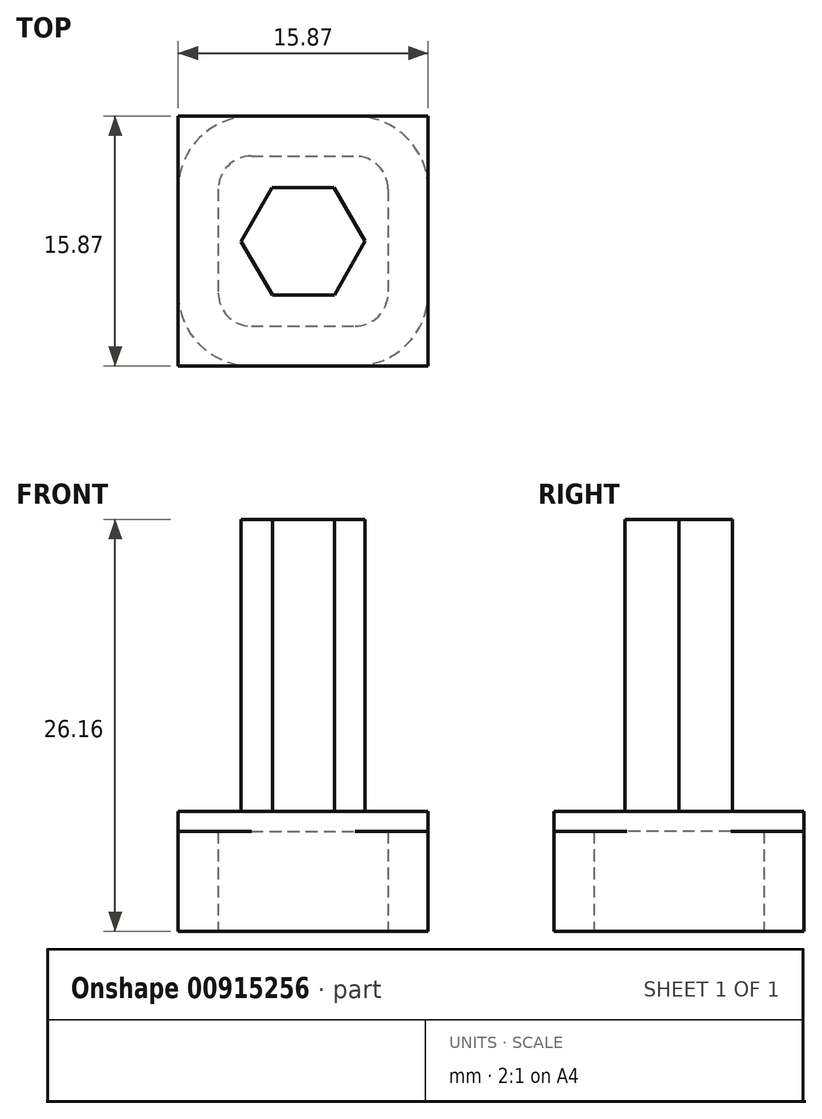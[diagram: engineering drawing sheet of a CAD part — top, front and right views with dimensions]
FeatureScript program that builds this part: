
annotation { "Feature Type Name" : "Feature", "Feature Type Description" : "" }
export const myFeature = defineFeature(function(context is Context, id is Id, definition is map)
    precondition{}
    {
        {
            var Q0;
            Q0=qCreatedBy(makeId("Top.planeOp"),FACE);
            var sketch = newSketch(context, id + "F0", { "sketchPlane" : qUnion([Q0])});
            skLineSegment(sketch, "E0.bottom", {"start": v(2.09, 6.62) * mm, "end": v(8.66, 6.62) * mm});
            skLineSegment(sketch, "E0.top", {"start": v(2.09, -9.25) * mm, "end": v(8.66, -9.25) * mm});
            skLineSegment(sketch, "E0.left", {"start": v(-2.56, 1.97) * mm, "end": v(-2.56, -4.6) * mm});
            skLineSegment(sketch, "E0.right", {"start": v(13.31, 1.97) * mm, "end": v(13.31, -4.6) * mm});
            skPoint(sketch, "E1.visualSharp", {"position": v(-2.56, 6.62) * mm});
            skArc(sketch, "E1.filletArc", {"start": v(2.09, 6.62) * mm, "mid": v(-1.2, 5.26) * mm, "end": v(-2.56, 1.97) * mm});
            skPoint(sketch, "E2.visualSharp", {"position": v(13.31, 6.62) * mm});
            skArc(sketch, "E2.filletArc", {"start": v(13.31, 1.97) * mm, "mid": v(11.95, 5.26) * mm, "end": v(8.66, 6.62) * mm});
            skPoint(sketch, "E3.visualSharp", {"position": v(13.31, -9.25) * mm});
            skArc(sketch, "E3.filletArc", {"start": v(8.66, -9.25) * mm, "mid": v(11.95, -7.9) * mm, "end": v(13.31, -4.6) * mm});
            skPoint(sketch, "E4.visualSharp", {"position": v(-2.56, -9.25) * mm});
            skArc(sketch, "E4.filletArc", {"start": v(-2.56, -4.6) * mm, "mid": v(-1.2, -7.9) * mm, "end": v(2.09, -9.25) * mm});
            skArc(sketch, "E5.0", {"start": v(2.09, 4.08) * mm, "mid": v(0.6, 3.46) * mm, "end": v(-0.02, 1.97) * mm});
            skLineSegment(sketch, "E5.1", {"start": v(-0.02, 1.97) * mm, "end": v(-0.02, -4.6) * mm});
            skLineSegment(sketch, "E5.2", {"start": v(2.09, 4.08) * mm, "end": v(8.66, 4.08) * mm});
            skArc(sketch, "E5.3", {"start": v(-0.02, -4.6) * mm, "mid": v(0.6, -6.1) * mm, "end": v(2.09, -6.71) * mm});
            skArc(sketch, "E5.4", {"start": v(10.77, 1.97) * mm, "mid": v(10.16, 3.46) * mm, "end": v(8.66, 4.08) * mm});
            skLineSegment(sketch, "E5.5", {"start": v(10.77, 1.97) * mm, "end": v(10.77, -4.6) * mm});
            skArc(sketch, "E5.6", {"start": v(8.66, -6.71) * mm, "mid": v(10.16, -6.1) * mm, "end": v(10.77, -4.6) * mm});
            skLineSegment(sketch, "E5.7", {"start": v(2.09, -6.71) * mm, "end": v(8.66, -6.71) * mm});
            skSolve(sketch);
        }
        {
            var Q0;
            Q0=makeQuery(id+"F0.imprint","IMPRINT",FACE,{"disambiguationData":[TD([[makeQuery(id+"F0.imprint","IMPRINT",EDGE,{"derivedFrom":sQuery(id+"F0.wireOp",EDGE,"E0.bottom")}),-1.0]])]});
            extrude(context, id + "F1", {"entities" : qUnion([Q0]), "depth" : 6.35 * mm, "offsetDistance" : 25.4 * mm});
        }
        {
            var Q0;
            Q0=makeQuery(id+"F1.opExtrude","CAP_FACE",FACE,{"disambiguationData":[OSD([sQuery(id+"F0.wireOp",EDGE,"E0.bottom"),sQuery(id+"F0.wireOp",EDGE,"E0.top"),sQuery(id+"F0.wireOp",EDGE,"E0.left"),sQuery(id+"F0.wireOp",EDGE,"E0.right"),sQuery(id+"F0.wireOp",EDGE,"E1.filletArc"),sQuery(id+"F0.wireOp",EDGE,"E2.filletArc"),sQuery(id+"F0.wireOp",EDGE,"E3.filletArc"),sQuery(id+"F0.wireOp",EDGE,"E4.filletArc"),sQuery(id+"F0.wireOp",EDGE,"E5.0"),sQuery(id+"F0.wireOp",EDGE,"E5.1"),sQuery(id+"F0.wireOp",EDGE,"E5.2"),sQuery(id+"F0.wireOp",EDGE,"E5.3"),sQuery(id+"F0.wireOp",EDGE,"E5.4"),sQuery(id+"F0.wireOp",EDGE,"E5.5"),sQuery(id+"F0.wireOp",EDGE,"E5.6"),sQuery(id+"F0.wireOp",EDGE,"E5.7")])],"isStart":false});
            var sketch = newSketch(context, id + "F2", { "sketchPlane" : qUnion([Q0])});
            skLineSegment(sketch, "E6.bottom", {"start": v(-2.56, 6.62) * mm, "end": v(13.31, 6.62) * mm});
            skLineSegment(sketch, "E6.top", {"start": v(-2.56, -9.25) * mm, "end": v(13.31, -9.25) * mm});
            skLineSegment(sketch, "E6.left", {"start": v(-2.56, 6.62) * mm, "end": v(-2.56, -9.25) * mm});
            skLineSegment(sketch, "E6.right", {"start": v(13.31, 6.62) * mm, "end": v(13.31, -9.25) * mm});
            skSolve(sketch);
        }
        {
            var Q0;
            Q0=makeQuery(id+"F2.imprint","IMPRINT",FACE,{"disambiguationData":[TD([[makeQuery(id+"F2.imprint","IMPRINT",EDGE,{"derivedFrom":makeQuery(id+"F1.opExtrude","CAP_EDGE",EDGE,{"disambiguationData":[OSD([sQuery(id+"F0.wireOp",EDGE,"E5.0")])],"isStart":false})}),1.0]])]});
            var Q1;
            {var subQ2=makeQuery(id+"F1.opExtrude","CAP_EDGE",EDGE,{"disambiguationData":[OSD([sQuery(id+"F0.wireOp",EDGE,"E1.filletArc")])],"isStart":false});Q1=makeQuery(id+"F2.imprint","IMPRINT",FACE,{"disambiguationData":[TD([[makeQuery(id+"F2.imprint","IMPRINT",EDGE,{"derivedFrom":subQ2}),1.0]])]});}
            var Q2;
            {var subQ1=makeQuery(id+"F1.opExtrude","CAP_EDGE",EDGE,{"disambiguationData":[OSD([sQuery(id+"F0.wireOp",EDGE,"E1.filletArc")])],"isStart":false});Q2=makeQuery(id+"F2.imprint","IMPRINT",FACE,{"disambiguationData":[TD([[makeQuery(id+"F2.imprint","IMPRINT",EDGE,{"derivedFrom":subQ1}),-1.0]])]});}
            var Q3;
            {var subQ1=makeQuery(id+"F1.opExtrude","CAP_EDGE",EDGE,{"disambiguationData":[OSD([sQuery(id+"F0.wireOp",EDGE,"E4.filletArc")])],"isStart":false});Q3=makeQuery(id+"F2.imprint","IMPRINT",FACE,{"disambiguationData":[TD([[makeQuery(id+"F2.imprint","IMPRINT",EDGE,{"derivedFrom":subQ1}),-1.0]])]});}
            var Q4;
            {var subQ1=makeQuery(id+"F1.opExtrude","CAP_EDGE",EDGE,{"disambiguationData":[OSD([sQuery(id+"F0.wireOp",EDGE,"E3.filletArc")])],"isStart":false});Q4=makeQuery(id+"F2.imprint","IMPRINT",FACE,{"disambiguationData":[TD([[makeQuery(id+"F2.imprint","IMPRINT",EDGE,{"derivedFrom":subQ1}),-1.0]])]});}
            var Q5;
            {var subQ1=makeQuery(id+"F1.opExtrude","CAP_EDGE",EDGE,{"disambiguationData":[OSD([sQuery(id+"F0.wireOp",EDGE,"E2.filletArc")])],"isStart":false});Q5=makeQuery(id+"F2.imprint","IMPRINT",FACE,{"disambiguationData":[TD([[makeQuery(id+"F2.imprint","IMPRINT",EDGE,{"derivedFrom":subQ1}),-1.0]])]});}
            extrude(context, id + "F3", {"entities" : qUnion([Q0, Q1, Q2, Q3, Q4, Q5]), "operationType" : NewBodyOperationType.ADD, "depth" : 1.27 * mm, "offsetDistance" : 25.4 * mm});
        }
        {
            var Q0;
            Q0=makeQuery(id+"F3.opExtrude","CAP_FACE",FACE,{"disambiguationData":[OSD([sQuery(id+"F2.wireOp",EDGE,"E6.bottom"),sQuery(id+"F2.wireOp",EDGE,"E6.top"),sQuery(id+"F2.wireOp",EDGE,"E6.left"),sQuery(id+"F2.wireOp",EDGE,"E6.right")])],"isStart":false});
            var sketch = newSketch(context, id + "F4", { "sketchPlane" : qUnion([Q0])});
            skCircle(sketch, "E7.cCircle", {"center": v(5.38, -1.33) * mm, "radius": 3.41 * mm, "construction": true});
            skLineSegment(sketch, "E7.0", {"start": v(1.43, -1.34) * mm, "end": v(3.4, 2.08) * mm});
            skLineSegment(sketch, "E7.1", {"start": v(3.4, 2.08) * mm, "end": v(7.34, 2.09) * mm});
            skLineSegment(sketch, "E7.2", {"start": v(7.34, 2.09) * mm, "end": v(9.32, -1.32) * mm});
            skLineSegment(sketch, "E7.3", {"start": v(9.32, -1.32) * mm, "end": v(7.35, -4.74) * mm});
            skLineSegment(sketch, "E7.4", {"start": v(7.35, -4.74) * mm, "end": v(3.41, -4.75) * mm});
            skLineSegment(sketch, "E7.5", {"start": v(3.41, -4.75) * mm, "end": v(1.43, -1.34) * mm});
            skPoint(sketch, "E7.0.midPoint", {"position": v(2.42, 0.37) * mm});
            skSolve(sketch);
        }
        {
            var Q0;
            Q0=makeQuery(id+"F4.imprint","IMPRINT",FACE,{"disambiguationData":[TD([[makeQuery(id+"F4.imprint","IMPRINT",EDGE,{"derivedFrom":sQuery(id+"F4.wireOp",EDGE,"E7.0")}),-1.0]])]});
            extrude(context, id + "F5", {"entities" : qUnion([Q0]), "operationType" : NewBodyOperationType.ADD, "depth" : 18.54 * mm, "offsetDistance" : 25.4 * mm});
        }
    });
